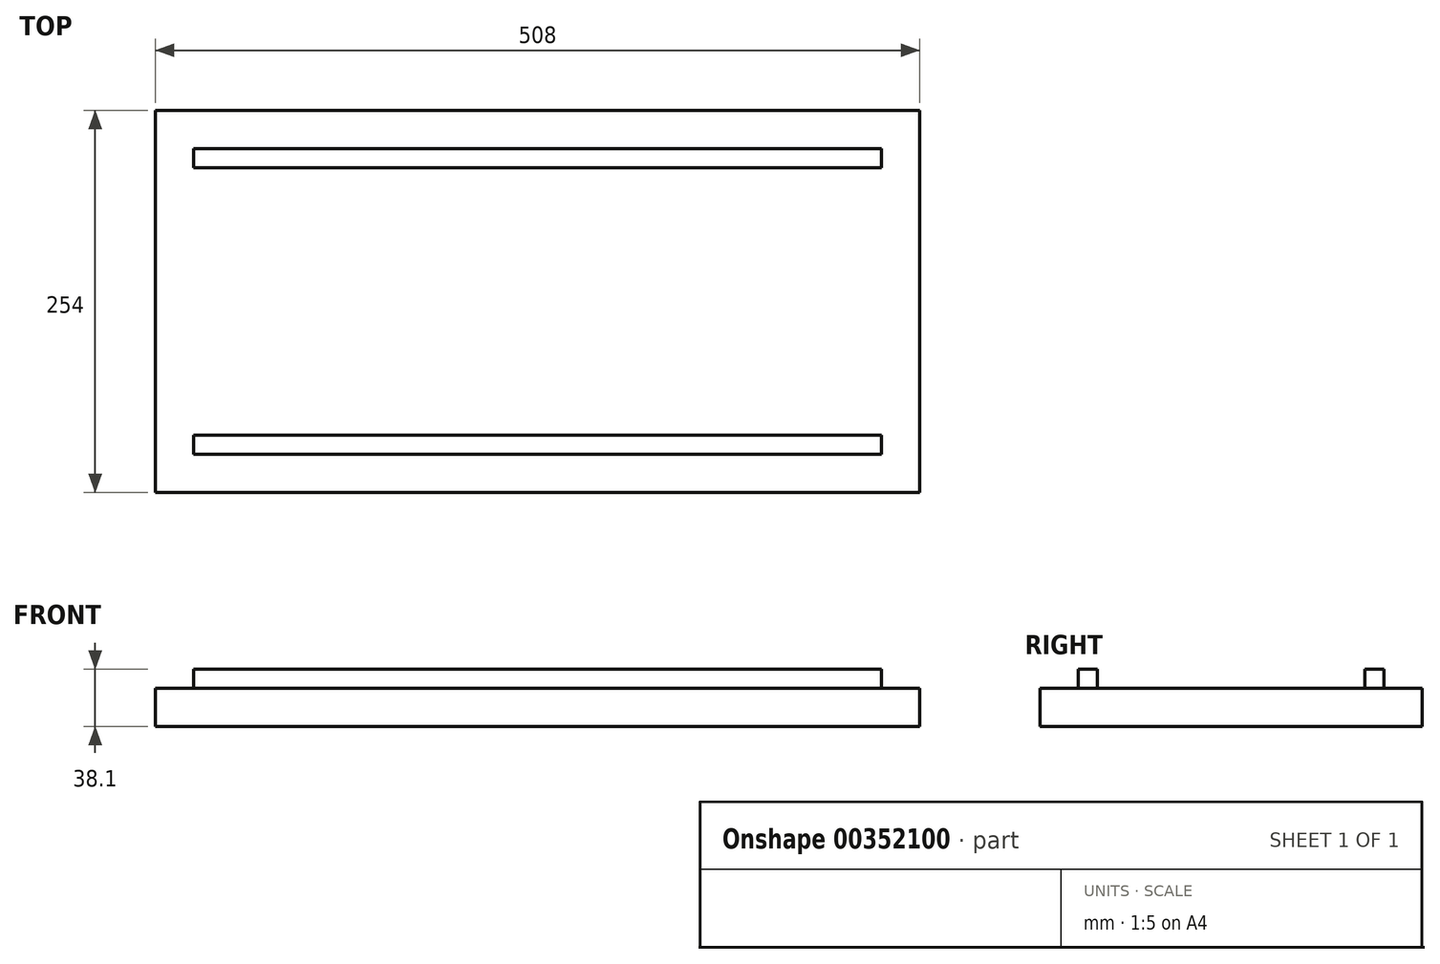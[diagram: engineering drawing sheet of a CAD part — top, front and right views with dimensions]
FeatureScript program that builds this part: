
annotation { "Feature Type Name" : "Feature", "Feature Type Description" : "" }
export const myFeature = defineFeature(function(context is Context, id is Id, definition is map)
    precondition{}
    {
        {
            var Q0;
            Q0=qCreatedBy(makeId("Top.planeOp"),FACE);
            var sketch = newSketch(context, id + "F0", { "sketchPlane" : qUnion([Q0])});
            skLineSegment(sketch, "E0.bottom", {"start": v(254, -127) * mm, "end": v(-254, -127) * mm});
            skLineSegment(sketch, "E0.top", {"start": v(254, 127) * mm, "end": v(-254, 127) * mm});
            skLineSegment(sketch, "E0.left", {"start": v(254, -127) * mm, "end": v(254, 127) * mm});
            skLineSegment(sketch, "E0.right", {"start": v(-254, -127) * mm, "end": v(-254, 127) * mm});
            skPoint(sketch, "E0.middle", {"position": v(0, 0) * mm});
            skSolve(sketch);
        }
        {
            var Q0;
            Q0=makeQuery(id+"F0.imprint","IMPRINT",FACE,{"disambiguationData":[TD([[makeQuery(id+"F0.imprint","IMPRINT",EDGE,{"derivedFrom":sQuery(id+"F0.wireOp",EDGE,"E0.bottom")}),-1.0]])]});
            extrude(context, id + "F1", {"entities" : qUnion([Q0]), "depth" : 25.4 * mm});
        }
        {
            var Q0;
            Q0=makeQuery(id+"F1.opExtrude","CAP_FACE",FACE,{"disambiguationData":[OSD([sQuery(id+"F0.wireOp",EDGE,"E0.bottom"),sQuery(id+"F0.wireOp",EDGE,"E0.top"),sQuery(id+"F0.wireOp",EDGE,"E0.left"),sQuery(id+"F0.wireOp",EDGE,"E0.right")])],"isStart":false});
            var sketch = newSketch(context, id + "F2", { "sketchPlane" : qUnion([Q0])});
            skLineSegment(sketch, "E1.bottom", {"start": v(-228.6, 101.6) * mm, "end": v(228.6, 101.6) * mm});
            skLineSegment(sketch, "E1.top", {"start": v(-228.6, 88.9) * mm, "end": v(228.6, 88.9) * mm});
            skLineSegment(sketch, "E1.left", {"start": v(-228.6, 101.6) * mm, "end": v(-228.6, 88.9) * mm});
            skLineSegment(sketch, "E1.right", {"start": v(228.6, 101.6) * mm, "end": v(228.6, 88.9) * mm});
            skLineSegment(sketch, "E2.bottom", {"start": v(-228.6, -88.9) * mm, "end": v(228.6, -88.9) * mm});
            skLineSegment(sketch, "E2.top", {"start": v(-228.6, -101.6) * mm, "end": v(228.6, -101.6) * mm});
            skLineSegment(sketch, "E2.left", {"start": v(-228.6, -88.9) * mm, "end": v(-228.6, -101.6) * mm});
            skLineSegment(sketch, "E2.right", {"start": v(228.6, -88.9) * mm, "end": v(228.6, -101.6) * mm});
            skSolve(sketch);
        }
        {
            var Q0;
            Q0 = qSketchRegion(id + "F2", true);
            extrude(context, id + "F3", {"entities" : qUnion([Q0]), "operationType" : NewBodyOperationType.ADD, "depth" : 12.7 * mm});
        }
    });
